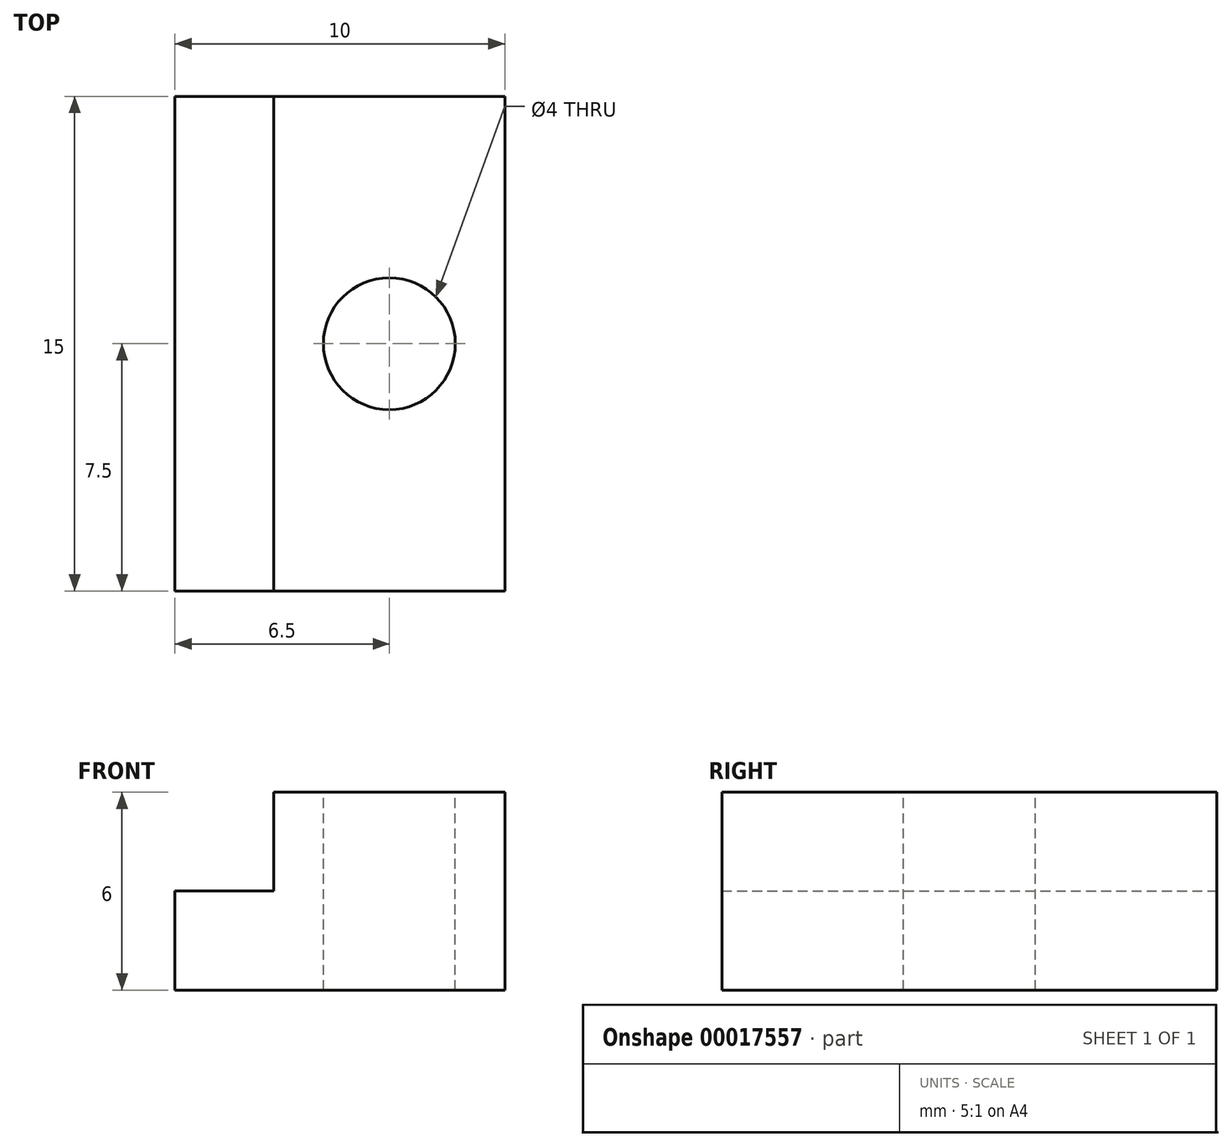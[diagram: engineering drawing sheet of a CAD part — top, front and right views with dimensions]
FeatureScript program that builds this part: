
annotation { "Feature Type Name" : "Feature", "Feature Type Description" : "" }
export const myFeature = defineFeature(function(context is Context, id is Id, definition is map)
    precondition{}
    {
        {
            var Q0;
            Q0=qCreatedBy(makeId("Top.planeOp"),FACE);
            var sketch = newSketch(context, id + "F0", { "sketchPlane" : qUnion([Q0])});
            skLineSegment(sketch, "E0.bottom", {"start": v(0, 0) * mm, "end": v(10, 0) * mm});
            skLineSegment(sketch, "E0.top", {"start": v(0, 15) * mm, "end": v(10, 15) * mm});
            skLineSegment(sketch, "E0.left", {"start": v(0, 0) * mm, "end": v(0, 15) * mm});
            skLineSegment(sketch, "E0.right", {"start": v(10, 0) * mm, "end": v(10, 15) * mm});
            skSolve(sketch);
        }
        {
            var Q0;
            Q0=qSketchRegion(id+"F0",true);
            extrude(context, id + "F1", {"entities" : qUnion([Q0]), "depth" : 6 * mm});
        }
        {
            var Q0;
            Q0=makeQuery(id+"F1.opExtrude","CAP_FACE",FACE,{"disambiguationData":[OSD([sQuery(id+"F0.wireOp",EDGE,"E0.bottom"),sQuery(id+"F0.wireOp",EDGE,"E0.top"),sQuery(id+"F0.wireOp",EDGE,"E0.left"),sQuery(id+"F0.wireOp",EDGE,"E0.right")])],"isStart":false});
            var sketch = newSketch(context, id + "F2", { "sketchPlane" : qUnion([Q0])});
            skLineSegment(sketch, "E1.bottom", {"start": v(0, 15) * mm, "end": v(3, 15) * mm});
            skLineSegment(sketch, "E1.top", {"start": v(0, 0) * mm, "end": v(3, 0) * mm});
            skLineSegment(sketch, "E1.left", {"start": v(0, 15) * mm, "end": v(0, 0) * mm});
            skLineSegment(sketch, "E1.right", {"start": v(3, 15) * mm, "end": v(3, 0) * mm});
            skSolve(sketch);
        }
        {
            var Q0;
            Q0=qSketchRegion(id+"F2",true);
            extrude(context, id + "F3", {"entities" : qUnion([Q0]), "operationType" : NewBodyOperationType.REMOVE, "oppositeDirection" : true, "depth" : 3 * mm});
        }
        {
            var Q0;
            Q0=makeQuery(id+"F1.opExtrude","CAP_FACE",FACE,{"disambiguationData":[OSD([sQuery(id+"F0.wireOp",EDGE,"E0.bottom"),sQuery(id+"F0.wireOp",EDGE,"E0.top"),sQuery(id+"F0.wireOp",EDGE,"E0.left"),sQuery(id+"F0.wireOp",EDGE,"E0.right")])],"isStart":false});
            var sketch = newSketch(context, id + "F4", { "sketchPlane" : qUnion([Q0])});
            skCircle(sketch, "E2", {"center": v(6.5, 7.5) * mm, "radius": 2 * mm});
            skPoint(sketch, "E3", {"position": v(6.5, 15) * mm});
            skPoint(sketch, "E4", {"position": v(10, 7.5) * mm});
            skSolve(sketch);
        }
        {
            var Q0;
            Q0=qSketchRegion(id+"F4",true);
            extrude(context, id + "F5", {"entities" : qUnion([Q0]), "operationType" : NewBodyOperationType.REMOVE, "oppositeDirection" : true, "depth" : 25 * mm});
        }
    });
